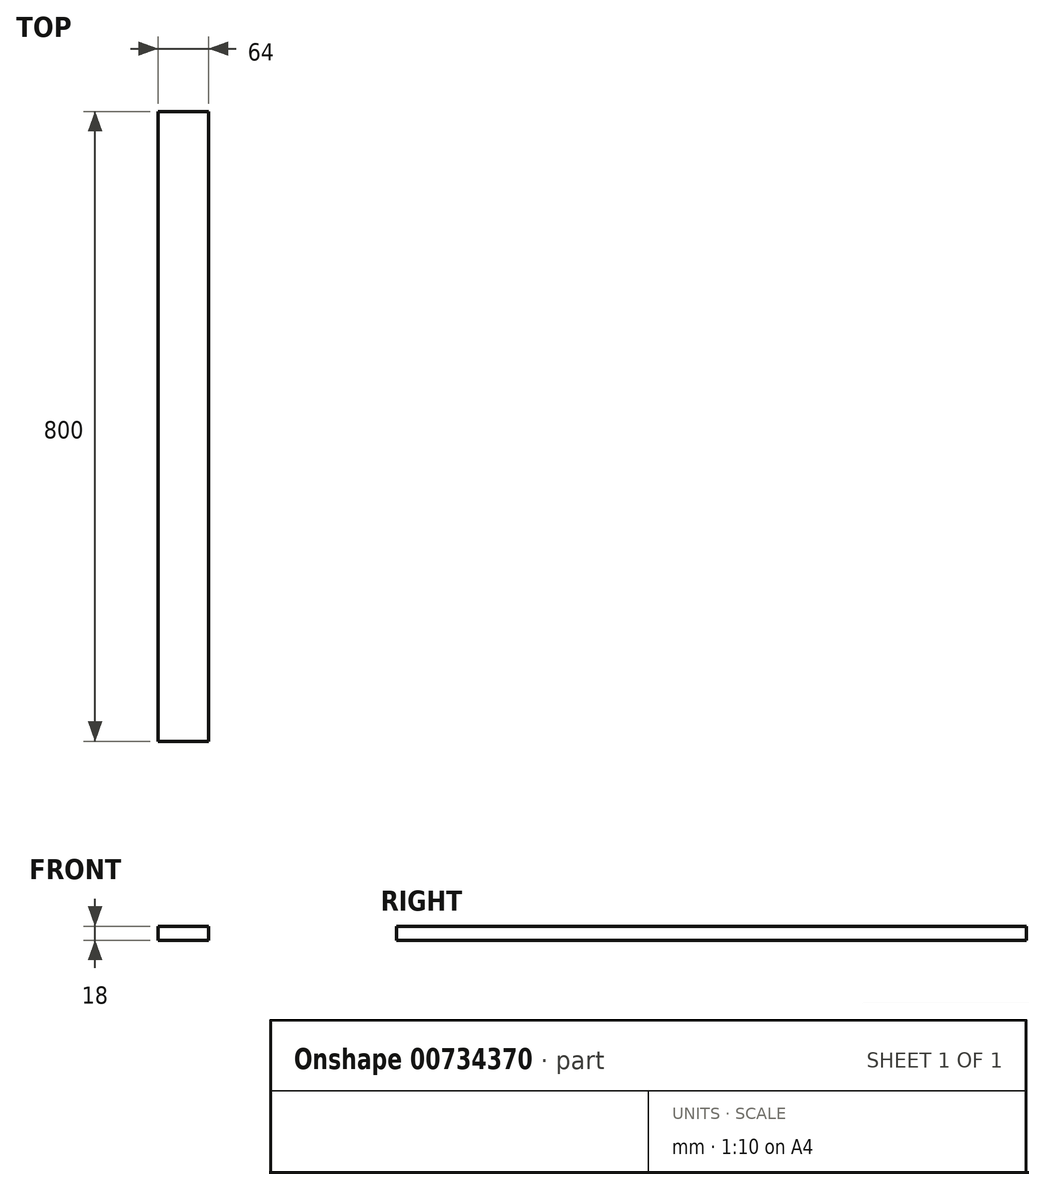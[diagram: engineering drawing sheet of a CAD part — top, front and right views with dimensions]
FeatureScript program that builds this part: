
annotation { "Feature Type Name" : "Feature", "Feature Type Description" : "" }
export const myFeature = defineFeature(function(context is Context, id is Id, definition is map)
    precondition{}
    {
        {
            var Q0;
            Q0=qCreatedBy(makeId("Top.planeOp"),FACE);
            var sketch = newSketch(context, id + "F0", { "sketchPlane" : qUnion([Q0])});
            skLineSegment(sketch, "E0.bottom", {"start": v(-32, -400) * mm, "end": v(32, -400) * mm});
            skLineSegment(sketch, "E0.top", {"start": v(-32, 400) * mm, "end": v(32, 400) * mm});
            skLineSegment(sketch, "E0.left", {"start": v(-32, -400) * mm, "end": v(-32, 400) * mm});
            skLineSegment(sketch, "E0.right", {"start": v(32, -400) * mm, "end": v(32, 400) * mm});
            skPoint(sketch, "E0.middle", {"position": v(0, 0) * mm});
            skSolve(sketch);
        }
        {
            var Q0;
            Q0 = qSketchRegion(id + "F0", true);
            extrude(context, id + "F1", {"entities" : qUnion([Q0]), "depth" : 18 * mm, "offsetDistance" : 25 * mm});
        }
    });
